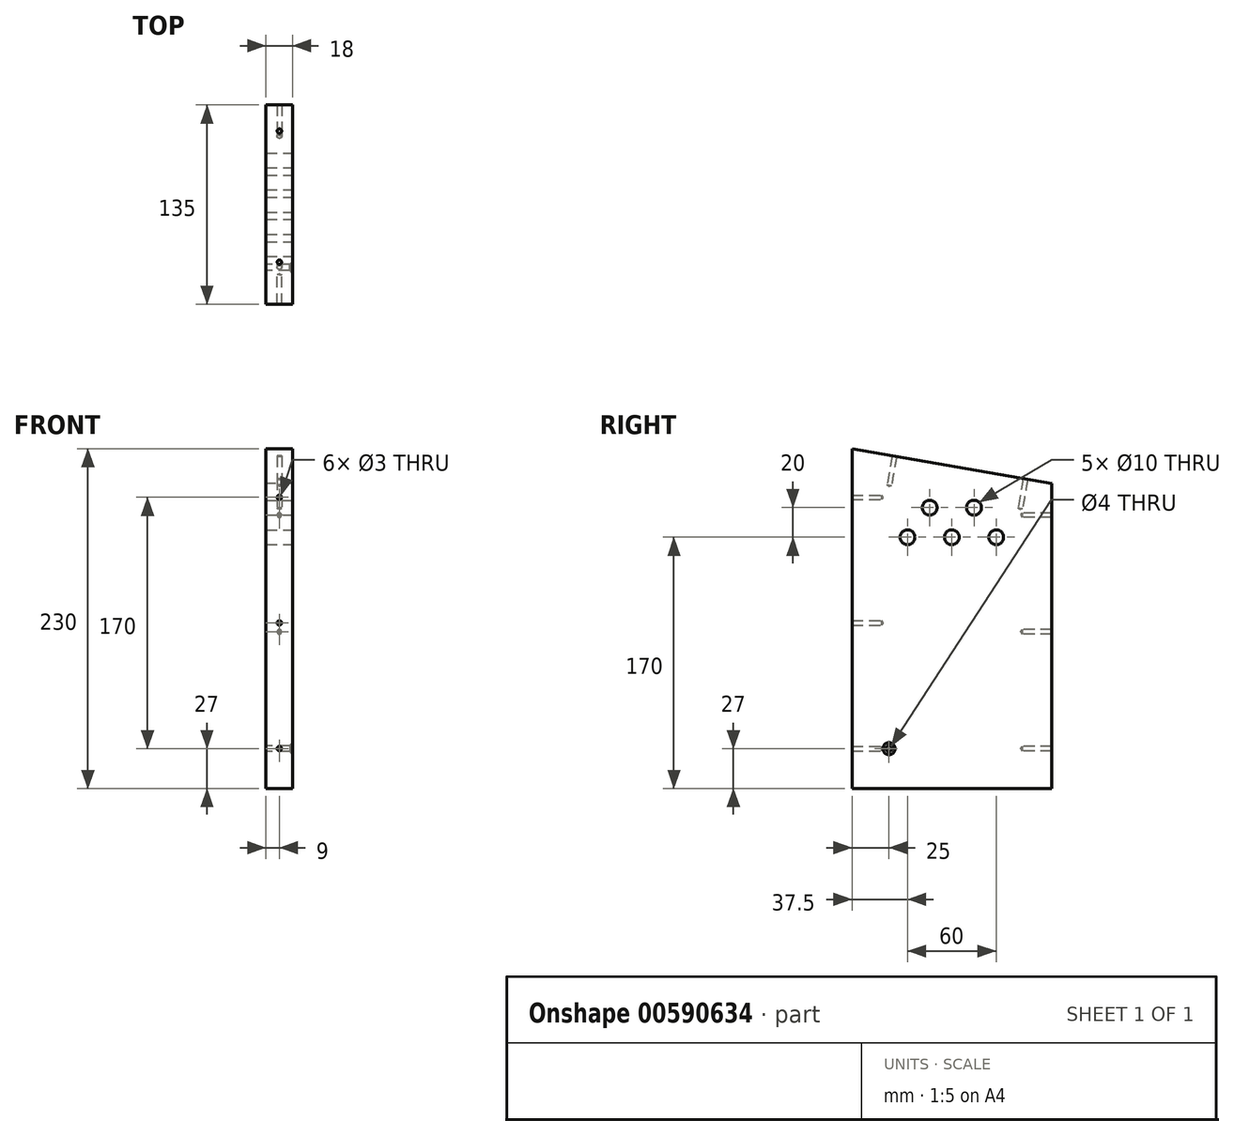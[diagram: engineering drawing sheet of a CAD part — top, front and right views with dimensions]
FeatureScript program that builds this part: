
annotation { "Feature Type Name" : "Feature", "Feature Type Description" : "" }
export const myFeature = defineFeature(function(context is Context, id is Id, definition is map)
    precondition{}
    {
        {
            var Q0;
            Q0=qCreatedBy(makeId("Right.planeOp"),FACE);
            var sketch = newSketch(context, id + "F0", { "sketchPlane" : qUnion([Q0])});
            skLineSegment(sketch, "E0", {"start": v(0, 0) * mm, "end": v(0, 230) * mm});
            skLineSegment(sketch, "E1", {"start": v(0, 230) * mm, "end": v(135, 206.2) * mm});
            skLineSegment(sketch, "E2", {"start": v(135, 206.2) * mm, "end": v(135, 0) * mm});
            skLineSegment(sketch, "E3", {"start": v(135, 0) * mm, "end": v(0, 0) * mm});
            skPoint(sketch, "E4", {"position": v(67.5, 170) * mm});
            skPoint(sketch, "E5", {"position": v(37.5, 170) * mm});
            skPoint(sketch, "E6", {"position": v(97.5, 170) * mm});
            skPoint(sketch, "E7", {"position": v(52.5, 190) * mm});
            skPoint(sketch, "E8", {"position": v(82.5, 190) * mm});
            skPoint(sketch, "E9", {"position": v(67.5, 0) * mm});
            skSolve(sketch);
        }
        {
            var Q0;
            Q0=makeQuery(id+"F0.imprint","IMPRINT",FACE,{"disambiguationData":[TD([[makeQuery(id+"F0.imprint","IMPRINT",EDGE,{"derivedFrom":sQuery(id+"F0.wireOp",EDGE,"E0")}),-1.0]])]});
            extrude(context, id + "F1", {"entities" : qUnion([Q0]), "depth" : 18 * mm, "offsetDistance" : 25 * mm});
        }
        {
            var Q0;
            Q0=sQuery(id+"F0.wireOp",VERTEX,"E5");
            var Q1;
            Q1=sQuery(id+"F0.wireOp",VERTEX,"E4");
            var Q2;
            Q2=sQuery(id+"F0.wireOp",VERTEX,"E6");
            var Q3;
            Q3=makeQuery(id+"F1.opExtrude","SWEPT_BODY",BODY,{"disambiguationData":[OSD([sQuery(id+"F0.wireOp",EDGE,"E0"),sQuery(id+"F0.wireOp",EDGE,"E1"),sQuery(id+"F0.wireOp",EDGE,"E2"),sQuery(id+"F0.wireOp",EDGE,"E3")])]});
            hole(context, id + "F2", {"style" : HoleStyle.SIMPLE, "endStyle" : HoleEndStyle.THROUGH, "oppositeDirection" : true, "holeDiameter" : 10 * mm, "majorDiameter" : 5 * mm, "isTappedThrough" : true, "tappedDepth" : 12 * mm, "tapClearance" : 3, "locations" : qUnion([Q0, Q1, Q2]), "scope" : qUnion([Q3])});
        }
        {
            var Q0;
            Q0=sQuery(id+"F0.wireOp",VERTEX,"E7");
            var Q1;
            Q1=sQuery(id+"F0.wireOp",VERTEX,"E8");
            var Q2;
            Q2=makeQuery(id+"F1.opExtrude","SWEPT_BODY",BODY,{"disambiguationData":[OSD([sQuery(id+"F0.wireOp",EDGE,"E0"),sQuery(id+"F0.wireOp",EDGE,"E1"),sQuery(id+"F0.wireOp",EDGE,"E2"),sQuery(id+"F0.wireOp",EDGE,"E3")])]});
            hole(context, id + "F3", {"style" : HoleStyle.SIMPLE, "endStyle" : HoleEndStyle.THROUGH, "oppositeDirection" : true, "holeDiameter" : 10 * mm, "majorDiameter" : 5 * mm, "isTappedThrough" : true, "tappedDepth" : 12 * mm, "tapClearance" : 3, "locations" : qUnion([Q0, Q1]), "scope" : qUnion([Q2])});
        }
        {
            var Q0;
            Q0=makeQuery(id+"F1.opExtrude","CAP_FACE",FACE,{"disambiguationData":[OSD([sQuery(id+"F0.wireOp",EDGE,"E0"),sQuery(id+"F0.wireOp",EDGE,"E1"),sQuery(id+"F0.wireOp",EDGE,"E2"),sQuery(id+"F0.wireOp",EDGE,"E3")])],"isStart":false});
            var sketch = newSketch(context, id + "F4", { "sketchPlane" : qUnion([Q0])});
            skPoint(sketch, "E10", {"position": v(25, 27) * mm});
            skPoint(sketch, "E11", {"position": v(67.5, 0) * mm});
            skSolve(sketch);
        }
        {
            var Q0;
            Q0=sQuery(id+"F4.wireOp",VERTEX,"E10");
            var Q1;
            Q1=makeQuery(id+"F1.opExtrude","SWEPT_BODY",BODY,{"disambiguationData":[OSD([sQuery(id+"F0.wireOp",EDGE,"E0"),sQuery(id+"F0.wireOp",EDGE,"E1"),sQuery(id+"F0.wireOp",EDGE,"E2"),sQuery(id+"F0.wireOp",EDGE,"E3")])]});
            hole(context, id + "F5", {"style" : HoleStyle.C_SINK, "endStyle" : HoleEndStyle.THROUGH, "holeDiameter" : 4 * mm, "cSinkDiameter" : 8.2 * mm, "cSinkAngle" : 90 * degree, "majorDiameter" : 5 * mm, "isTappedThrough" : true, "tappedDepth" : 12 * mm, "tapClearance" : 3, "locations" : qUnion([Q0]), "scope" : qUnion([Q1])});
        }
        {
            var Q0;
            Q0=makeQuery(id+"F1.opExtrude","SWEPT_FACE",FACE,{"disambiguationData":[OSD([sQuery(id+"F0.wireOp",EDGE,"E2")])]});
            var sketch = newSketch(context, id + "F6", { "sketchPlane" : qUnion([Q0])});
            skPoint(sketch, "E12", {"position": v(-9, 27) * mm});
            skPoint(sketch, "E12.positionSnap0", {"position": v(-9, 0) * mm});
            skPoint(sketch, "E13", {"position": v(-9, 106) * mm});
            skPoint(sketch, "E14", {"position": v(-9, 185) * mm});
            skSolve(sketch);
        }
        {
            var Q0;
            Q0=sQuery(id+"F6.wireOp",VERTEX,"E12");
            var Q1;
            Q1=sQuery(id+"F6.wireOp",VERTEX,"E13");
            var Q2;
            Q2=sQuery(id+"F6.wireOp",VERTEX,"E14");
            var Q3;
            Q3=makeQuery(id+"F1.opExtrude","SWEPT_BODY",BODY,{"disambiguationData":[OSD([sQuery(id+"F0.wireOp",EDGE,"E0"),sQuery(id+"F0.wireOp",EDGE,"E1"),sQuery(id+"F0.wireOp",EDGE,"E2"),sQuery(id+"F0.wireOp",EDGE,"E3")])]});
            hole(context, id + "F7", {"style" : HoleStyle.SIMPLE, "endStyle" : HoleEndStyle.BLIND, "holeDiameter" : 3 * mm, "majorDiameter" : 5 * mm, "holeDepth" : 20 * mm, "isTappedThrough" : true, "tappedDepth" : 12 * mm, "tapClearance" : 3, "locations" : qUnion([Q0, Q1, Q2]), "scope" : qUnion([Q3])});
        }
        {
            var Q0;
            Q0=makeQuery(id+"F1.opExtrude","SWEPT_FACE",FACE,{"disambiguationData":[OSD([sQuery(id+"F0.wireOp",EDGE,"E0")])]});
            var sketch = newSketch(context, id + "F8", { "sketchPlane" : qUnion([Q0])});
            skPoint(sketch, "E15", {"position": v(9, 27) * mm});
            skPoint(sketch, "E15.positionSnap0", {"position": v(9, 0) * mm});
            skPoint(sketch, "E16", {"position": v(9, 112) * mm});
            skPoint(sketch, "E17", {"position": v(9, 197) * mm});
            skSolve(sketch);
        }
        {
            var Q0;
            Q0=sQuery(id+"F8.wireOp",VERTEX,"E17");
            var Q1;
            Q1=sQuery(id+"F8.wireOp",VERTEX,"E16");
            var Q2;
            Q2=sQuery(id+"F8.wireOp",VERTEX,"E15");
            var Q3;
            Q3=makeQuery(id+"F1.opExtrude","SWEPT_BODY",BODY,{"disambiguationData":[OSD([sQuery(id+"F0.wireOp",EDGE,"E0"),sQuery(id+"F0.wireOp",EDGE,"E1"),sQuery(id+"F0.wireOp",EDGE,"E2"),sQuery(id+"F0.wireOp",EDGE,"E3")])]});
            hole(context, id + "F9", {"style" : HoleStyle.SIMPLE, "endStyle" : HoleEndStyle.BLIND, "holeDiameter" : 3 * mm, "majorDiameter" : 5 * mm, "holeDepth" : 20 * mm, "isTappedThrough" : true, "tappedDepth" : 12 * mm, "tapClearance" : 3, "locations" : qUnion([Q0, Q1, Q2]), "scope" : qUnion([Q3])});
        }
        {
            var Q0;
            Q0=makeQuery(id+"F1.opExtrude","SWEPT_FACE",FACE,{"disambiguationData":[OSD([sQuery(id+"F0.wireOp",EDGE,"E1")])]});
            var sketch = newSketch(context, id + "F10", { "sketchPlane" : qUnion([Q0])});
            skPoint(sketch, "E18", {"position": v(9, 79.14) * mm});
            skPoint(sketch, "E18.positionSnap0", {"position": v(9, 97.14) * mm});
            skPoint(sketch, "E19", {"position": v(9, -10.86) * mm});
            skSolve(sketch);
        }
        {
            var Q0;
            Q0=sQuery(id+"F10.wireOp",VERTEX,"E19");
            var Q1;
            Q1=sQuery(id+"F10.wireOp",VERTEX,"E18");
            var Q2;
            Q2=makeQuery(id+"F1.opExtrude","SWEPT_BODY",BODY,{"disambiguationData":[OSD([sQuery(id+"F0.wireOp",EDGE,"E0"),sQuery(id+"F0.wireOp",EDGE,"E1"),sQuery(id+"F0.wireOp",EDGE,"E2"),sQuery(id+"F0.wireOp",EDGE,"E3")])]});
            hole(context, id + "F11", {"style" : HoleStyle.SIMPLE, "endStyle" : HoleEndStyle.BLIND, "holeDiameter" : 3 * mm, "majorDiameter" : 5 * mm, "holeDepth" : 20 * mm, "isTappedThrough" : true, "tappedDepth" : 12 * mm, "tapClearance" : 3, "locations" : qUnion([Q0, Q1]), "scope" : qUnion([Q2])});
        }
    });
